# Revit family: POR_Sans_K8223_BIM_FR
name_source: partatom
category: Plumbing Fixtures
revit_build: Autodesk Revit 2017 (Build: 20160225_1515(x64)
units: mm (PartAtom-declared; Revit-internal decimal feet)

## family parameters
Always vertical = No
Cut with Voids When Loaded = No
OmniClass Number = 23.45.05.21.11.21
OmniClass Title = Urinals
Part Type = Normal
Room Calculation Point = No
Round Connector Dimension = Use Diameter
Shared = No
Work Plane-Based = No

## types (1)
- K822367 - ACCESSOIRES SIPHON H P/URINOIR
    Accessoires = www.idealstandard.be
    Auteur = Ideal Standard
    BOSUseNativeGeometries = 1
    Bim-NomDuProjet = POR_Porcher_Cisterns_K822367
    Caractéristiques = Siphon sortie horizontale
    CodeBarre = 4015413066365
    ConseilsDInstallation = www.idealstandard.be
    Cost = 0 $
    Couleur = Blanc
    CoûtDeRemplacement = 0
    DateDeCréation = 2018_08_15
    Description = Siphon sortie horizontale
    Dimensions = 168 x 96 x 177mm
    DuréeGarantie = ans
    DétailGarantie = Constructeur
    Espace = Interne
    Forme = Complexe
    Hauteur = 168 mm
    IfcExportAs = IfcSanitaryTerminalType
    IfcExportType = Toilet Cisterns
    InformationsProduit = www.idealstandard.be
    Largeur = 96 mm  [stored 0.314961 ft]
    LienUtile = www.idealstandard.be
    Longueur = 177 mm
    Manufacturer = www.idealstandard.be
    Marque = PORCHER
    Model = K822367
    Nom = POR_Porcher_Cisterns_K822367
    PerformanceAccessibilité = NF
    PoidsNet = 0.16 Kg
    Profondeur = 0 mm  [stored 0 ft]
    Raccordement = Plomberie
    Référence = K822367
    Révision = 1
    TypeDImmobilisation = Fixe
    URL = www.idealstandard.be
    Uniclass2015Code = Pr_40_20_93_89
    Uniclass2015Title = WC cisterns
    Uniclass2015Version = Products v1.1
    UnitéDeTemps = an
    UrlDuFabricant = www.idealstandard.be
    Version = 1

note: [stored X ft] marks values corroborated as IEEE doubles in the binary element streams (Revit-internal decimal feet)

## geometry (parser evidence)
native form markers: Sweep x4
no freeform markers — native parametric forms only
